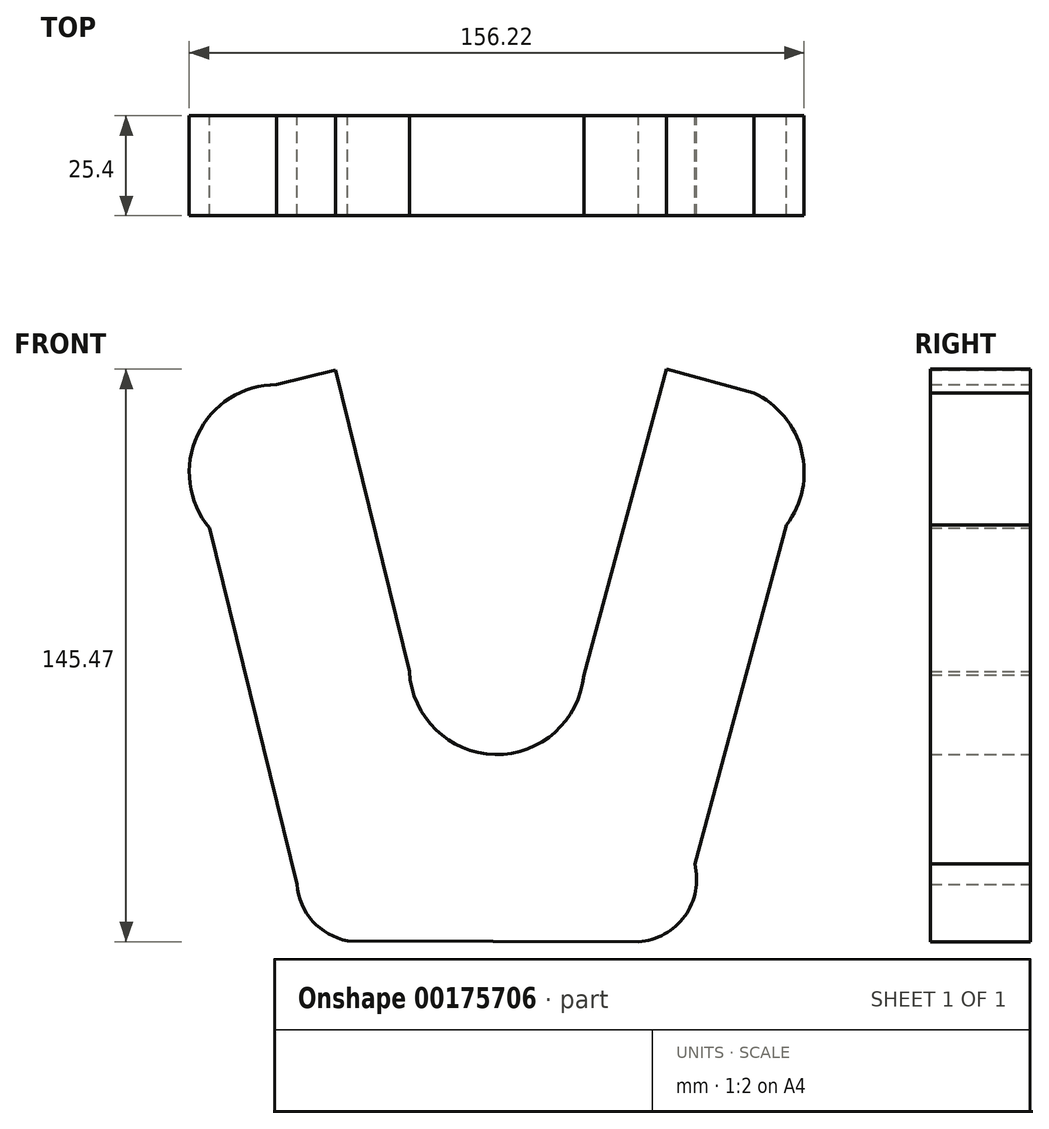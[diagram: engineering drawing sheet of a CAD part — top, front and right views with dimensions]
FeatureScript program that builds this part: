
annotation { "Feature Type Name" : "Feature", "Feature Type Description" : "" }
export const myFeature = defineFeature(function(context is Context, id is Id, definition is map)
    precondition{}
    {
        {
            var Q0;
            Q0=qCreatedBy(makeId("Front.planeOp"),FACE);
            var sketch = newSketch(context, id + "F0", { "sketchPlane" : qUnion([Q0])});
            skCircle(sketch, "E0", {"center": v(0, 0) * mm, "radius": 22.23 * mm});
            skCircle(sketch, "E1", {"center": v(34.93, -53.97) * mm, "radius": 15.88 * mm});
            skCircle(sketch, "E2", {"center": v(55.88, 49.53) * mm, "radius": 22.23 * mm});
            skCircle(sketch, "E3", {"center": v(-34.93, -53.98) * mm, "radius": 15.88 * mm});
            skCircle(sketch, "E4", {"center": v(-55.88, 49.53) * mm, "radius": 22.23 * mm});
            skLineSegment(sketch, "E5", {"start": v(20.15, -9.37) * mm, "end": v(34.47, 43.57) * mm});
            skLineSegment(sketch, "E6", {"start": v(73.61, 36.13) * mm, "end": v(50.3, -50.05) * mm});
            skLineSegment(sketch, "E7", {"start": v(34.47, 43.57) * mm, "end": v(43.15, 75.66) * mm});
            skLineSegment(sketch, "E8", {"start": v(43.15, 75.66) * mm, "end": v(65.28, 69.67) * mm});
            skLineSegment(sketch, "E9", {"start": v(35.99, -69.81) * mm, "end": v(-37.85, -69.58) * mm});
            skLineSegment(sketch, "E10", {"start": v(-50.75, -55.2) * mm, "end": v(-72.95, 35.3) * mm});
            skLineSegment(sketch, "E11", {"start": v(-33.87, 46.45) * mm, "end": v(-20.2, -9.26) * mm});
            skLineSegment(sketch, "E12", {"start": v(-33.87, 46.45) * mm, "end": v(-40.97, 75.41) * mm});
            skLineSegment(sketch, "E13", {"start": v(-40.97, 75.41) * mm, "end": v(-55.88, 71.76) * mm});
            skSolve(sketch);
        }
        {
            var Q0;
            {var subQ0=sQuery(id+"F0.wireOp",EDGE,"E13");Q0=makeQuery(id+"F0.imprint","IMPRINT",FACE,{"disambiguationData":[TD([[makeQuery(id+"F0.imprint","IMPRINT",EDGE,{"derivedFrom":subQ0}),1.0]])]});}
            var Q1;
            {var subQ7=sQuery(id+"F0.wireOp",EDGE,"E6");Q1=makeQuery(id+"F0.imprint","IMPRINT",FACE,{"disambiguationData":[TD([[makeQuery(id+"F0.imprint","IMPRINT",EDGE,{"derivedFrom":subQ7}),-1.0]])]});}
            var Q2;
            {var subQ0=sQuery(id+"F0.wireOp",EDGE,"E8");var subQ1=sQuery(id+"F0.wireOp",EDGE,"E2");var subQ2=makeQuery(id+"F0.imprint","INTERSECT",VERTEX,{"disambiguationData":[OD(1.0)],"derivedFrom":[subQ1,subQ0]});Q2=makeQuery(id+"F0.imprint","IMPRINT",FACE,{"disambiguationData":[TD([[makeQuery(id+"F0.imprint","IMPRINT",EDGE,{"disambiguationData":[TD([[subQ2,-1.0]])],"derivedFrom":subQ1}),-1.0]])]});}
            var Q3;
            {var subQ1=sQuery(id+"F0.wireOp",EDGE,"E2");var subQ5=sQuery(id+"F0.wireOp",EDGE,"E8");var subQ7=makeQuery(id+"F0.imprint","INTERSECT",VERTEX,{"disambiguationData":[OD(1.0)],"derivedFrom":[subQ1,subQ5]});Q3=makeQuery(id+"F0.imprint","IMPRINT",FACE,{"disambiguationData":[TD([[makeQuery(id+"F0.imprint","IMPRINT",EDGE,{"disambiguationData":[TD([[subQ7,-1.0]])],"derivedFrom":subQ1}),1.0]])]});}
            var Q4;
            {var subQ0=sQuery(id+"F0.wireOp",EDGE,"E1");var subQ1=makeQuery(id+"F0.imprint","INTERSECT",VERTEX,{"derivedFrom":[subQ0,sQuery(id+"F0.wireOp",EDGE,"E6")]});Q4=makeQuery(id+"F0.imprint","IMPRINT",FACE,{"disambiguationData":[TD([[makeQuery(id+"F0.imprint","IMPRINT",EDGE,{"disambiguationData":[TD([[subQ1,-1.0]])],"derivedFrom":subQ0}),1.0]])]});}
            var Q5;
            {var subQ0=sQuery(id+"F0.wireOp",EDGE,"E9");var subQ1=sQuery(id+"F0.wireOp",EDGE,"E3");var subQ2=makeQuery(id+"F0.imprint","INTERSECT",VERTEX,{"disambiguationData":[OD(0.0)],"derivedFrom":[subQ1,subQ0]});Q5=makeQuery(id+"F0.imprint","IMPRINT",FACE,{"disambiguationData":[TD([[makeQuery(id+"F0.imprint","IMPRINT",EDGE,{"disambiguationData":[TD([[subQ2,1.0]])],"derivedFrom":subQ1}),1.0]])]});}
            var Q6;
            {var subQ0=sQuery(id+"F0.wireOp",EDGE,"E4");var subQ1=makeQuery(id+"F0.imprint","INTERSECT",VERTEX,{"derivedFrom":[subQ0,sQuery(id+"F0.wireOp",EDGE,"E13")]});Q6=makeQuery(id+"F0.imprint","IMPRINT",FACE,{"disambiguationData":[TD([[makeQuery(id+"F0.imprint","IMPRINT",EDGE,{"disambiguationData":[TD([[subQ1,1.0]])],"derivedFrom":subQ0}),1.0]])]});}
            extrude(context, id + "F1", {"entities" : qUnion([Q0, Q1, Q2, Q3, Q4, Q5, Q6]), "depth" : 25.4 * mm});
        }
    });
